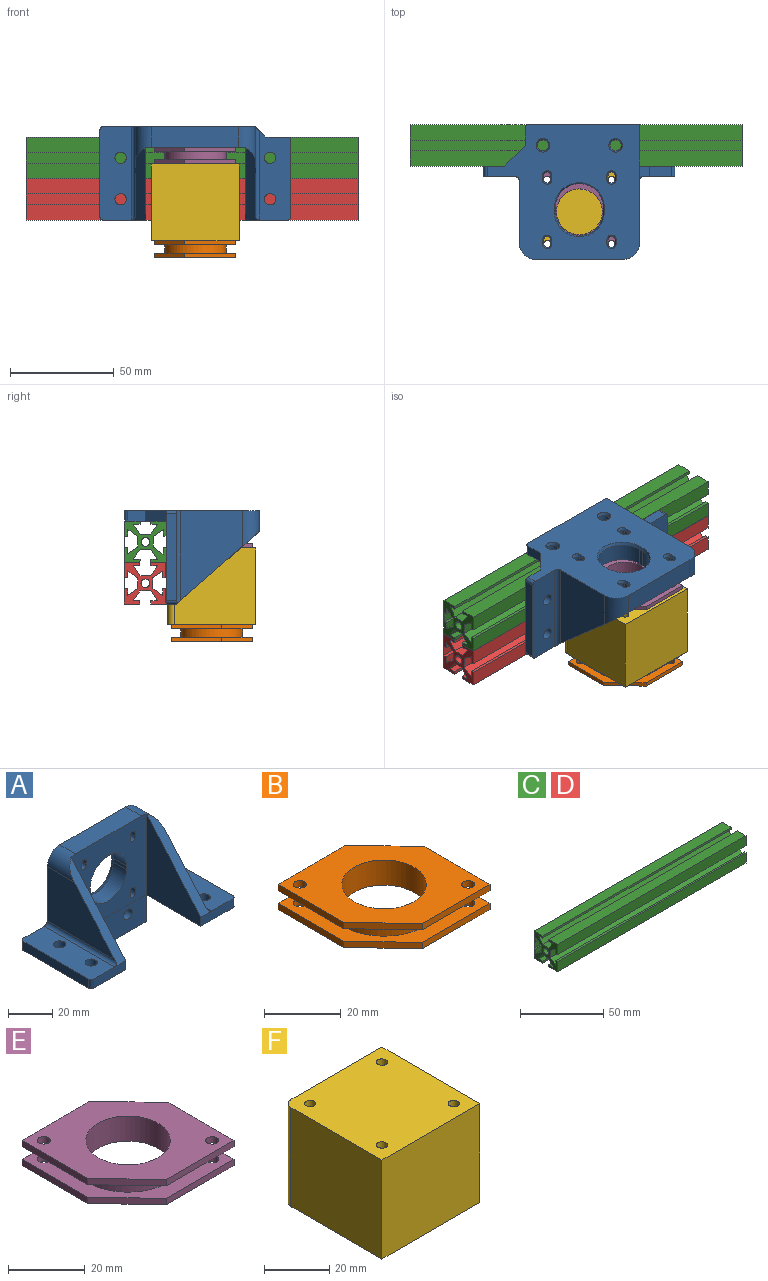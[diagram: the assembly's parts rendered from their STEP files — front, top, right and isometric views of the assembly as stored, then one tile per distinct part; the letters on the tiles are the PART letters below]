
ASSEMBLY  parts=6 mates=6
PART A: 80 faces, bbox 92x45x65 mm
  f0: plane 43.25x30mm, normal (1,0,0), area 903.7mm2, adj f1,f21,f52,f78
  f1: plane 39.42x34.49mm, normal (0,-0.75,0.66), area 249.4mm2, adj f0,f3,f49,f52,f78
  f2: plane 92x45mm, normal (0,0,-1), area 1965.5mm2, adj f3,f5,f6,f7,f8,f9,f17,f21
  f3: plane 20.5x5mm, normal (0,-1,0), area 102.5mm2, adj f1,f2,f38,f46,f49
  f4: plane 39.42x34.49mm, normal (0,-0.75,0.66), area 249.4mm2, adj f5,f48,f50,f53,f79
  f5: plane 20.5x5mm, normal (0,-1,0), area 102.5mm2, adj f2,f4,f41,f43,f48
  f6: cylinder r=2.75mm len=5.5mm, axis (0,0,1), area 86.4mm2, adj f2,f41
  f7: cylinder r=2.75mm len=5.5mm, axis (0,0,1), area 86.4mm2, adj f2,f41
  f8: cylinder r=2.75mm len=5.5mm, axis (0,0,1), area 86.4mm2, adj f2,f38
  f9: cylinder r=2.75mm len=5.5mm, axis (0,0,1), area 86.4mm2, adj f2,f38
  f10: cylinder r=2.75mm len=5.5mm, axis (0,1,0), area 60.5mm2, adj f17,f75
  f11: cylinder r=2.75mm len=5.5mm, axis (0,1,0), area 60.5mm2, adj f17,f76
  f12: cylinder r=1.7mm len=8.5mm, axis (0,1,0), area 45.4mm2, adj f35,f36,f47,f74
  f13: cylinder r=1.7mm len=8.5mm, axis (0,1,0), area 45.4mm2, adj f32,f33,f47,f70
  f14: cylinder r=1.7mm len=8.5mm, axis (0,1,0), area 45.4mm2, adj f28,f30,f47,f62
  f15: cylinder r=1.7mm len=8.5mm, axis (0,1,0), area 45.4mm2, adj f26,f27,f47,f66
  f16: cylinder r=11.5mm len=23mm, axis (0,1,0), area 307.1mm2, adj f23,f24,f47,f58
  f17: plane 65x20mm, normal (0,-1,0), area 1102mm2, adj f2,f10,f11,f18,f20,f45,f51,f54
  f18: plane 8.5x5mm, normal (-1,0,0), area 42.5mm2, adj f17,f21,f45,f54
  f19: plane 42x10mm, normal (0,0,1), area 420mm2, adj f21,f47,f52,f53
  f20: plane 53.5x5mm, normal (0,0,-1), area 267.5mm2, adj f17,f21,f45,f51
  f21: plane 73.5x65mm, normal (0,1,0), area 3138.8mm2, adj f0,f2,f18,f19,f20,f41,f44,f45
  f22: cylinder r=11.5mm len=23mm, axis (0,1,0), area 307.1mm2, adj f23,f24,f47,f55
  f23: plane 8.5x2mm, normal (-1,0,0), area 17mm2, adj f16,f22,f47,f57
  f24: plane 8.5x2mm, normal (1,0,0), area 17mm2, adj f16,f22,f47,f56
  f25: cylinder r=1.7mm len=8.5mm, axis (0,1,0), area 45.4mm2, adj f26,f27,f47,f63
  f26: plane 8.5x2mm, normal (-1,0,0), area 17mm2, adj f15,f25,f47,f65
  f27: plane 8.5x2mm, normal (1,0,0), area 17mm2, adj f15,f25,f47,f64
  f28: plane 8.5x2mm, normal (1,0,0), area 17mm2, adj f14,f29,f47,f60
  f29: cylinder r=1.7mm len=8.5mm, axis (0,1,0), area 45.4mm2, adj f28,f30,f47,f59
  f30: plane 8.5x2mm, normal (-1,0,0), area 17mm2, adj f14,f29,f47,f61
  f31: cylinder r=1.7mm len=8.5mm, axis (0,1,0), area 45.4mm2, adj f32,f33,f47,f67
  f32: plane 8.5x2mm, normal (-1,0,0), area 17mm2, adj f13,f31,f47,f69
  f33: plane 8.5x2mm, normal (1,0,0), area 17mm2, adj f13,f31,f47,f68
  f34: cylinder r=1.7mm len=8.5mm, axis (0,1,0), area 45.4mm2, adj f35,f36,f47,f71
  f35: plane 8.5x2mm, normal (-1,0,0), area 17mm2, adj f12,f34,f47,f73
  f36: plane 8.5x2mm, normal (1,0,0), area 17mm2, adj f12,f34,f47,f72
  f37: plane 37x5mm, normal (1,0,0), area 185mm2, adj f2,f38,f42,f46
  f38: plane 43x15mm, normal (0,0,1), area 556mm2, adj f3,f8,f9,f37,f39,f42,f46,f77
  f39: plane 10.5x5mm, normal (0,1,0), area 52.5mm2, adj f2,f38,f42,f77
  f40: plane 42x5mm, normal (-1,0,0), area 210mm2, adj f2,f41,f43,f44
  f41: plane 45x15mm, normal (0,0,1), area 626.5mm2, adj f5,f6,f7,f21,f40,f43,f44,f79
  f42: cylinder r=1.5mm len=5mm, axis (0,0,-1), area 11.8mm2, adj f2,f37,f38,f39
  f43: cylinder r=1.5mm len=5mm, axis (0,0,-1), area 11.8mm2, adj f2,f5,f40,f41
  f44: cylinder r=1.5mm len=5mm, axis (0,0,1), area 11.8mm2, adj f2,f21,f40,f41
  f45: cylinder r=1.5mm len=5mm, axis (0,-1,0), area 11.8mm2, adj f17,f18,f20,f21
  f46: cylinder r=1.5mm len=5mm, axis (0,0,-1), area 11.8mm2, adj f2,f3,f37,f38
  f47: plane 48x45mm, normal (0,-1,0), area 1633.9mm2, adj f2,f12,f13,f14,f15,f16,f19,f22
  f48: plane 44.42x35mm, normal (1,0,0), area 874.9mm2, adj f2,f4,f5,f47,f53
  f49: plane 44.42x35mm, normal (-1,0,0), area 874.9mm2, adj f1,f2,f3,f47,f52
  f50: plane 43.25x30mm, normal (-1,0,0), area 903.7mm2, adj f4,f21,f53,f79
  f51: plane 20x5mm, normal (1,0,0), area 100mm2, adj f2,f17,f20,f21
  f52: cylinder r=8mm len=17mm, axis (0,-1,0), area 157.1mm2, adj f0,f1,f19,f21,f47,f49
  f53: cylinder r=8mm len=17mm, axis (0,1,0), area 157.1mm2, adj f4,f19,f21,f47,f48,f50
  f54: plane 10x10mm, normal (-0.71,0,-0.71), area 70.7mm2, adj f2,f17,f18,f21
  f55: cone r=11.5mm half-angle=20deg, axis (0,1,0), area 59mm2, adj f21,f22,f56,f57
  f56: plane 2x1.5mm, normal (0.94,0.34,0), area 3.2mm2, adj f21,f24,f55,f58
  f57: plane 2x1.5mm, normal (-0.94,0.34,0), area 3.2mm2, adj f21,f23,f55,f58
  f58: cone r=11.5mm half-angle=20deg, axis (0,1,0), area 59mm2, adj f16,f21,f56,f57
  f59: cone r=1.7mm half-angle=20deg, axis (0,1,0), area 9.9mm2, adj f21,f29,f60,f61
  f60: plane 2x1.5mm, normal (0.94,0.34,0), area 3.2mm2, adj f21,f28,f59,f62
  f61: plane 2x1.5mm, normal (-0.94,0.34,0), area 3.2mm2, adj f21,f30,f59,f62
  f62: cone r=1.7mm half-angle=20deg, axis (0,1,0), area 9.9mm2, adj f14,f21,f60,f61
  f63: cone r=1.7mm half-angle=20deg, axis (0,1,0), area 9.9mm2, adj f21,f25,f64,f65
  f64: plane 2x1.5mm, normal (0.94,0.34,0), area 3.2mm2, adj f21,f27,f63,f66
  f65: plane 2x1.5mm, normal (-0.94,0.34,0), area 3.2mm2, adj f21,f26,f63,f66
  f66: cone r=1.7mm half-angle=20deg, axis (0,1,0), area 9.9mm2, adj f15,f21,f64,f65
  f67: cone r=1.7mm half-angle=20deg, axis (0,1,0), area 9.9mm2, adj f21,f31,f68,f69
  f68: plane 2x1.5mm, normal (0.94,0.34,0), area 3.2mm2, adj f21,f33,f67,f70
  f69: plane 2x1.5mm, normal (-0.94,0.34,0), area 3.2mm2, adj f21,f32,f67,f70
  f70: cone r=1.7mm half-angle=20deg, axis (0,1,0), area 9.9mm2, adj f13,f21,f68,f69
  f71: cone r=1.7mm half-angle=20deg, axis (0,1,0), area 9.9mm2, adj f21,f34,f72,f73
  f72: plane 2x1.5mm, normal (0.94,0.34,0), area 3.2mm2, adj f21,f36,f71,f74
  f73: plane 2x1.5mm, normal (-0.94,0.34,0), area 3.2mm2, adj f21,f35,f71,f74
  f74: cone r=1.7mm half-angle=20deg, axis (0,1,0), area 9.9mm2, adj f12,f21,f72,f73
  f75: cone r=2.75mm half-angle=20deg, axis (0,1,0), area 30.3mm2, adj f10,f21
  f76: cone r=2.75mm half-angle=20deg, axis (0,1,0), area 30.3mm2, adj f11,f21
  f77: plane 7x5mm, normal (0.71,0.71,0), area 36.6mm2, adj f2,f21,f38,f39,f78
  f78: cylinder r=2mm len=45mm, axis (0,-1,0), area 137.1mm2, adj f0,f1,f38,f77
  f79: cylinder r=2mm len=45mm, axis (0,-1,0), area 139.4mm2, adj f4,f21,f41,f50
PART B: 22 faces, bbox 39x39x8 mm
  f0: plane 24.92x2mm, normal (0,1,0), area 49.8mm2, adj f1,f5,f6,f7
  f1: plane 24.18x2mm, normal (-1,0,0), area 48.4mm2, adj f0,f2,f6,f7
  f2: plane 14.82x14.08mm, normal (-0.72,-0.69,0), area 40.9mm2, adj f1,f3,f6,f7
  f3: plane 24.92x2mm, normal (0,-1,0), area 49.8mm2, adj f2,f4,f6,f7
  f4: plane 24.18x2mm, normal (1,0,0), area 48.4mm2, adj f3,f5,f6,f7
  f5: plane 14.82x14.08mm, normal (0.72,0.69,0), area 40.9mm2, adj f0,f4,f6,f7
  f6: plane 39x39mm, normal (0,0,1), area 600.1mm2, adj f0,f1,f2,f3,f4,f5,f8,f9
  f7: plane 39x39mm, normal (0,0,-1), area 914.2mm2, adj f0,f1,f2,f3,f4,f5,f8,f9
  f8: cylinder r=1.7mm len=3.4mm, axis (0,0,-1), area 21.4mm2, adj f6,f7
  f9: cylinder r=1.7mm len=3.4mm, axis (0,0,-1), area 21.4mm2, adj f6,f7
  f10: cylinder r=11mm len=22mm, axis (0,0,-1), area 552.9mm2, adj f7,f20
  f11: cylinder r=14.86mm len=29.73mm, axis (0,0,-1), area 373.6mm2, adj f6,f21
  f12: plane 24.92x2mm, normal (0,1,0), area 49.8mm2, adj f13,f18,f20,f21
  f13: plane 24.18x2mm, normal (-1,0,0), area 48.4mm2, adj f12,f14,f20,f21
  f14: plane 14.82x14.08mm, normal (-0.72,-0.69,0), area 40.9mm2, adj f13,f15,f20,f21
  f15: plane 24.92x2mm, normal (0,-1,0), area 49.8mm2, adj f14,f16,f20,f21
  f16: plane 24.18x2mm, normal (1,0,0), area 48.4mm2, adj f15,f18,f20,f21
  f17: cylinder r=1.7mm len=3.4mm, axis (0,0,-1), area 21.4mm2, adj f20,f21
  f18: plane 14.82x14.08mm, normal (0.72,0.69,0), area 40.9mm2, adj f12,f16,f20,f21
  f19: cylinder r=1.7mm len=3.4mm, axis (0,0,-1), area 21.4mm2, adj f20,f21
  f20: plane 39x39mm, normal (0,0,1), area 914.2mm2, adj f10,f12,f13,f14,f15,f16,f17,f18
  f21: plane 39x39mm, normal (0,0,-1), area 600.1mm2, adj f11,f12,f13,f14,f15,f16,f17,f18
PART C: 39 faces, bbox 160x20x20 mm
  f0: plane 160x7.47mm, normal (0,0,1), area 1195.2mm2, adj f6,f7,f8,f15
  f1: plane 160x7.4mm, normal (0,0,-1), area 1184mm2, adj f6,f7,f8,f37
  f2: plane 160x7.44mm, normal (0,-1,0), area 1189.6mm2, adj f3,f7,f8,f29
  f3: plane 160x7.33mm, normal (0,0,1), area 1172.8mm2, adj f2,f7,f8,f9
  f4: plane 160x7.37mm, normal (0,-1,0), area 1178.4mm2, adj f5,f7,f8,f30
  f5: plane 160x7.4mm, normal (0,0,-1), area 1184mm2, adj f4,f7,f8,f36
  f6: plane 160x20mm, normal (0,1,0), area 3200mm2, adj f0,f1,f7,f8
  f7: plane 20x20mm, normal (1,0,0), area 191.8mm2, adj f0,f1,f2,f3,f4,f5,f6,f9
  f8: plane 20x20mm, normal (-1,0,0), area 191.8mm2, adj f0,f1,f2,f3,f4,f5,f6,f9
  f9: plane 160x1.5mm, normal (0,1,0.01), area 239.6mm2, adj f3,f7,f8,f10
  f10: plane 160x3.31mm, normal (0,0.01,-1), area 528.8mm2, adj f7,f8,f9,f11
  f11: plane 160x4.78mm, normal (0,0.82,0.57), area 930.2mm2, adj f7,f8,f10,f12
  f12: plane 160x5.2mm, normal (0,0,1), area 832mm2, adj f7,f8,f11,f13
  f13: plane 160x4.82mm, normal (0,-0.83,0.56), area 933.8mm2, adj f7,f8,f12,f14
  f14: plane 160x3.31mm, normal (0,0,-1), area 528.8mm2, adj f7,f8,f13,f15
  f15: plane 160x1.48mm, normal (0,-1,0), area 236.7mm2, adj f0,f7,f8,f14
  f16: plane 160x3.31mm, normal (0,-1,-0.01), area 528.8mm2, adj f7,f8,f17,f23
  f17: plane 160x4.78mm, normal (0,0.57,-0.82), area 930.2mm2, adj f7,f8,f16,f18
  f18: plane 160x5.2mm, normal (0,1,0), area 832mm2, adj f7,f8,f17,f19
  f19: plane 160x4.82mm, normal (0,0.56,0.83), area 933.8mm2, adj f7,f8,f18,f20
  f20: plane 160x3.31mm, normal (0,-1,0), area 528.8mm2, adj f7,f8,f19,f21
  f21: plane 160x1.48mm, normal (0,0,1), area 236.7mm2, adj f7,f8,f20,f22
  f22: plane 160x5.2mm, normal (0,-1,0), area 832mm2, adj f7,f8,f21,f23
  f23: plane 160x1.5mm, normal (0,0.01,-1), area 239.6mm2, adj f7,f8,f16,f22
  f24: plane 160x3.31mm, normal (0,1,0.01), area 528.8mm2, adj f7,f8,f25,f30
  f25: plane 160x4.78mm, normal (0,-0.57,0.82), area 930.2mm2, adj f7,f8,f24,f26
  f26: plane 160x5.2mm, normal (0,-1,0), area 832mm2, adj f7,f8,f25,f27
  f27: plane 160x4.82mm, normal (0,-0.56,-0.83), area 933.8mm2, adj f7,f8,f26,f28
  f28: plane 160x3.31mm, normal (0,1,0), area 528.8mm2, adj f7,f8,f27,f29
  f29: plane 160x1.44mm, normal (0,0,-1), area 231mm2, adj f2,f7,f8,f28
  f30: plane 160x1.46mm, normal (0,-0.01,1), area 234mm2, adj f4,f7,f8,f24
  f31: plane 160x3.31mm, normal (0,-0.01,1), area 528.8mm2, adj f7,f8,f32,f37
  f32: plane 160x4.78mm, normal (0,-0.82,-0.57), area 930.2mm2, adj f7,f8,f31,f33
  f33: plane 160x5.2mm, normal (0,0,-1), area 832mm2, adj f7,f8,f32,f34
  f34: plane 160x4.82mm, normal (0,0.83,-0.56), area 933.8mm2, adj f7,f8,f33,f35
  f35: plane 160x3.31mm, normal (0,0,1), area 528.8mm2, adj f7,f8,f34,f36
  f36: plane 160x1.48mm, normal (0,1,0), area 236.6mm2, adj f5,f7,f8,f35
  f37: plane 160x1.5mm, normal (0,-1,-0.01), area 239.6mm2, adj f1,f7,f8,f31
  f38: cylinder r=2.1mm len=160mm, axis (1,0,0), area 2111.2mm2, adj f7,f8
PART D: same geometry as C
PART E: 22 faces, bbox 39x39x8 mm
  f0: plane 24.92x2mm, normal (0,1,0), area 49.8mm2, adj f1,f5,f6,f7
  f1: plane 24.18x2mm, normal (-1,0,0), area 48.4mm2, adj f0,f2,f6,f7
  f2: plane 14.82x14.08mm, normal (-0.72,-0.69,0), area 40.9mm2, adj f1,f3,f6,f7
  f3: plane 24.92x2mm, normal (0,-1,0), area 49.8mm2, adj f2,f4,f6,f7
  f4: plane 24.18x2mm, normal (1,0,0), area 48.4mm2, adj f3,f5,f6,f7
  f5: plane 14.82x14.08mm, normal (0.72,0.69,0), area 40.9mm2, adj f0,f4,f6,f7
  f6: plane 39x39mm, normal (0,0,1), area 600.1mm2, adj f0,f1,f2,f3,f4,f5,f8,f9
  f7: plane 39x39mm, normal (0,0,-1), area 914.2mm2, adj f0,f1,f2,f3,f4,f5,f8,f9
  f8: cylinder r=1.7mm len=3.4mm, axis (0,0,-1), area 21.4mm2, adj f6,f7
  f9: cylinder r=1.7mm len=3.4mm, axis (0,0,-1), area 21.4mm2, adj f6,f7
  f10: cylinder r=11mm len=22mm, axis (0,0,-1), area 552.9mm2, adj f7,f20
  f11: cylinder r=14.86mm len=29.73mm, axis (0,0,-1), area 373.6mm2, adj f6,f21
  f12: plane 24.92x2mm, normal (0,1,0), area 49.8mm2, adj f13,f18,f20,f21
  f13: plane 24.18x2mm, normal (-1,0,0), area 48.4mm2, adj f12,f14,f20,f21
  f14: plane 14.82x14.08mm, normal (-0.72,-0.69,0), area 40.9mm2, adj f13,f15,f20,f21
  f15: plane 24.92x2mm, normal (0,-1,0), area 49.8mm2, adj f14,f16,f20,f21
  f16: plane 24.18x2mm, normal (1,0,0), area 48.4mm2, adj f15,f18,f20,f21
  f17: cylinder r=1.7mm len=3.4mm, axis (0,0,-1), area 21.4mm2, adj f20,f21
  f18: plane 14.82x14.08mm, normal (0.72,0.69,0), area 40.9mm2, adj f12,f16,f20,f21
  f19: cylinder r=1.7mm len=3.4mm, axis (0,0,-1), area 21.4mm2, adj f20,f21
  f20: plane 39x39mm, normal (0,0,1), area 914.2mm2, adj f10,f12,f13,f14,f15,f16,f17,f18
  f21: plane 39x39mm, normal (0,0,-1), area 600.1mm2, adj f11,f12,f13,f14,f15,f16,f17,f18
PART F: 11 faces, bbox 42.3x42.3x37 mm
  f0: plane 39.3x37mm, normal (0,1,0), area 1454.1mm2, adj f3,f4,f5,f10
  f1: plane 39.3x37mm, normal (-1,0,0), area 1454.1mm2, adj f2,f4,f5,f10
  f2: plane 42.3x37mm, normal (0,-1,0), area 1565.1mm2, adj f1,f3,f4,f5
  f3: plane 42.3x37mm, normal (1,0,0), area 1565.1mm2, adj f0,f2,f4,f5
  f4: plane 42.3x42.3mm, normal (0,0,1), area 1751mm2, adj f0,f1,f2,f3,f6,f7,f8,f9
  f5: plane 42.3x42.3mm, normal (0,0,-1), area 1751mm2, adj f0,f1,f2,f3,f6,f7,f8,f9
  f6: cylinder r=1.7mm len=37mm, axis (0,0,1), area 395.2mm2, adj f4,f5
  f7: cylinder r=1.7mm len=37mm, axis (0,0,1), area 395.2mm2, adj f4,f5
  f8: cylinder r=1.7mm len=37mm, axis (0,0,1), area 395.2mm2, adj f4,f5
  f9: cylinder r=1.7mm len=37mm, axis (0,0,1), area 395.2mm2, adj f4,f5
  f10: cylinder r=3mm len=37mm, axis (0,0,1), area 174.4mm2, adj f0,f1,f4,f5
PLACE A rot(axis=(1,0,0),90deg) t=(-17.83,2.73,73.15)mm
PLACE B t=(-17.83,2.73,-21.85)mm
PLACE C t=(-39.45,1.58,28.15)mm
PLACE D t=(-39.45,1.65,8.15)mm
PLACE E t=(-17.83,2.73,68.15)mm
PLACE F t=(-17.85,2.75,23.15)mm
MATE planar A.f2 <-> C.f2  axis (0,1,0) through (-18.68,24.73,55.99)mm
MATE planar F.f4 <-> E.f10  axis (0,0,1) through (-17.83,2.73,60.15)mm
MATE planar A.f17 <-> C.f0  axis (0,0,-1) through (-17.65,34.42,73.15)mm
MATE planar B.f10 <-> F.f5  axis (0,0,1) through (-17.83,2.73,23.15)mm
MATE planar E.f10 <-> A.f16  axis (0,0,1) through (-17.83,2.73,68.15)mm
MATE planar D.f3 <-> C.f5  axis (0,0,1) through (-19.45,32.13,53.15)mm
